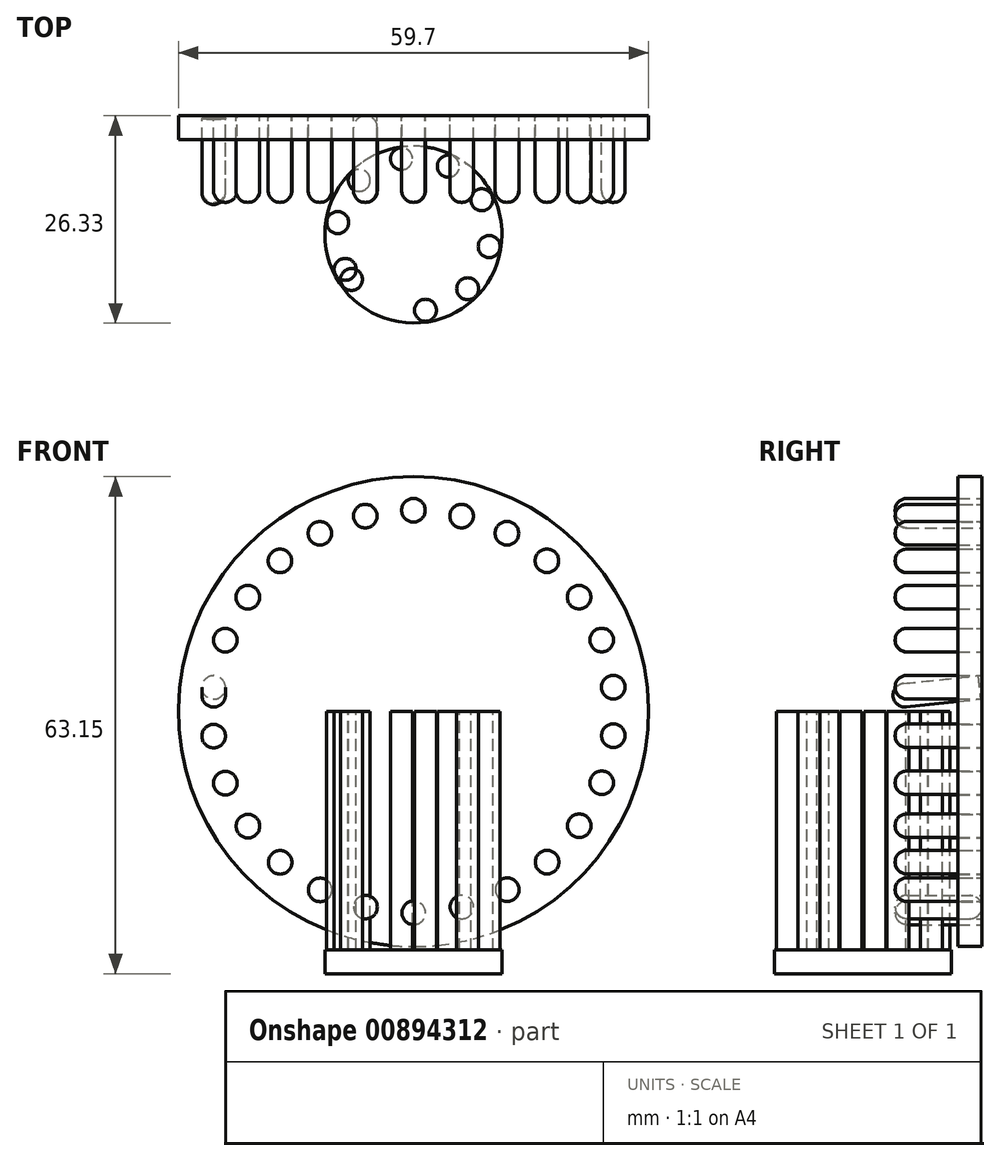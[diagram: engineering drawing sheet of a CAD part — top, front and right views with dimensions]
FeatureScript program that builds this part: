
annotation { "Feature Type Name" : "Feature", "Feature Type Description" : "" }
export const myFeature = defineFeature(function(context is Context, id is Id, definition is map)
    precondition{}
    {
        {
            var Q0;
            Q0=qCreatedBy(makeId("Front.planeOp"),FACE);
            var sketch = newSketch(context, id + "F0", { "sketchPlane" : qUnion([Q0])});
            skCircle(sketch, "E0", {"center": v(-25.57, 0) * mm, "radius": 1.5 * mm});
            skCircle(sketch, "E1.1.0", {"center": v(-25.38, 3.08) * mm, "radius": 1.5 * mm});
            skCircle(sketch, "E1.2.0", {"center": v(-24.83, 6.12) * mm, "radius": 1.5 * mm});
            skCircle(sketch, "E1.3.0", {"center": v(-23.91, 9.07) * mm, "radius": 1.5 * mm});
            skCircle(sketch, "E1.4.0", {"center": v(-22.64, 11.88) * mm, "radius": 1.5 * mm});
            skCircle(sketch, "E1.5.0", {"center": v(-21.05, 14.52) * mm, "radius": 1.5 * mm});
            skCircle(sketch, "E1.6.0", {"center": v(-19.14, 16.95) * mm, "radius": 1.5 * mm});
            skCircle(sketch, "E1.7.0", {"center": v(-16.96, 19.14) * mm, "radius": 1.5 * mm});
            skCircle(sketch, "E1.8.0", {"center": v(-14.53, 21.04) * mm, "radius": 1.5 * mm});
            skCircle(sketch, "E1.9.0", {"center": v(-11.89, 22.64) * mm, "radius": 1.5 * mm});
            skCircle(sketch, "E1.10.0", {"center": v(-9.07, 23.9) * mm, "radius": 1.5 * mm});
            skCircle(sketch, "E1.11.0", {"center": v(-6.13, 24.83) * mm, "radius": 1.5 * mm});
            skCircle(sketch, "E1.12.0", {"center": v(-3.1, 25.38) * mm, "radius": 1.5 * mm});
            skCircle(sketch, "E1.13.0", {"center": v(0, 25.57) * mm, "radius": 1.5 * mm});
            skCircle(sketch, "E1.14.0", {"center": v(3.07, 25.39) * mm, "radius": 1.5 * mm});
            skCircle(sketch, "E1.15.0", {"center": v(6.1, 24.83) * mm, "radius": 1.5 * mm});
            skCircle(sketch, "E1.16.0", {"center": v(9.06, 23.91) * mm, "radius": 1.5 * mm});
            skCircle(sketch, "E1.17.0", {"center": v(11.87, 22.65) * mm, "radius": 1.5 * mm});
            skCircle(sketch, "E1.18.0", {"center": v(14.52, 21.05) * mm, "radius": 1.5 * mm});
            skCircle(sketch, "E1.19.0", {"center": v(16.95, 19.15) * mm, "radius": 1.5 * mm});
            skCircle(sketch, "E1.20.0", {"center": v(19.13, 16.97) * mm, "radius": 1.5 * mm});
            skCircle(sketch, "E1.21.0", {"center": v(21.04, 14.54) * mm, "radius": 1.5 * mm});
            skCircle(sketch, "E1.22.0", {"center": v(22.64, 11.9) * mm, "radius": 1.5 * mm});
            skCircle(sketch, "E1.23.0", {"center": v(23.9, 9.08) * mm, "radius": 1.5 * mm});
            skCircle(sketch, "E1.24.0", {"center": v(24.82, 6.14) * mm, "radius": 1.5 * mm});
            skCircle(sketch, "E1.25.0", {"center": v(25.38, 3.1) * mm, "radius": 1.5 * mm});
            skCircle(sketch, "E1.26.0", {"center": v(25.57, 0.02) * mm, "radius": 1.5 * mm});
            skCircle(sketch, "E1.27.0", {"center": v(25.39, -3.06) * mm, "radius": 1.5 * mm});
            skCircle(sketch, "E1.28.0", {"center": v(24.83, -6.1) * mm, "radius": 1.5 * mm});
            skCircle(sketch, "E1.29.0", {"center": v(23.92, -9.05) * mm, "radius": 1.5 * mm});
            skCircle(sketch, "E1.30.0", {"center": v(22.65, -11.87) * mm, "radius": 1.5 * mm});
            skCircle(sketch, "E1.31.0", {"center": v(21.06, -14.5) * mm, "radius": 1.5 * mm});
            skCircle(sketch, "E1.32.0", {"center": v(19.15, -16.94) * mm, "radius": 1.5 * mm});
            skCircle(sketch, "E1.33.0", {"center": v(16.97, -19.13) * mm, "radius": 1.5 * mm});
            skCircle(sketch, "E1.34.0", {"center": v(14.54, -21.03) * mm, "radius": 1.5 * mm});
            skCircle(sketch, "E1.35.0", {"center": v(11.9, -22.63) * mm, "radius": 1.5 * mm});
            skCircle(sketch, "E1.36.0", {"center": v(9.1, -23.9) * mm, "radius": 1.5 * mm});
            skCircle(sketch, "E1.37.0", {"center": v(6.14, -24.82) * mm, "radius": 1.5 * mm});
            skCircle(sketch, "E1.38.0", {"center": v(3.1, -25.38) * mm, "radius": 1.5 * mm});
            skCircle(sketch, "E1.39.0", {"center": v(0.03, -25.57) * mm, "radius": 1.5 * mm});
            skCircle(sketch, "E1.40.0", {"center": v(-3.06, -25.39) * mm, "radius": 1.5 * mm});
            skCircle(sketch, "E1.41.0", {"center": v(-6.1, -24.83) * mm, "radius": 1.5 * mm});
            skCircle(sketch, "E1.42.0", {"center": v(-9.04, -23.92) * mm, "radius": 1.5 * mm});
            skCircle(sketch, "E1.43.0", {"center": v(-11.86, -22.66) * mm, "radius": 1.5 * mm});
            skCircle(sketch, "E1.44.0", {"center": v(-14.5, -21.06) * mm, "radius": 1.5 * mm});
            skCircle(sketch, "E1.45.0", {"center": v(-16.93, -19.16) * mm, "radius": 1.5 * mm});
            skCircle(sketch, "E1.46.0", {"center": v(-19.12, -16.98) * mm, "radius": 1.5 * mm});
            skCircle(sketch, "E1.47.0", {"center": v(-21.03, -14.55) * mm, "radius": 1.5 * mm});
            skCircle(sketch, "E1.48.0", {"center": v(-22.63, -11.91) * mm, "radius": 1.5 * mm});
            skCircle(sketch, "E1.49.0", {"center": v(-23.9, -9.1) * mm, "radius": 1.5 * mm});
            skCircle(sketch, "E1.50.0", {"center": v(-24.82, -6.15) * mm, "radius": 1.5 * mm});
            skLineSegment(sketch, "E1.anchor1", {"start": v(0, 0) * mm, "end": v(-25.57, 0) * mm, "construction": true});
            skLineSegment(sketch, "E1.anchor2", {"start": v(0, 0) * mm, "end": v(-25.38, -3.12) * mm, "construction": true});
            skCircle(sketch, "E2.1.51.0", {"center": v(-25.38, -3.12) * mm, "radius": 1.5 * mm});
            skCircle(sketch, "E3", {"center": v(0, 0) * mm, "radius": 29.85 * mm});
            skLineSegment(sketch, "E4", {"start": v(-29.85, 0) * mm, "end": v(29.85, 0.02) * mm});
            skSolve(sketch);
        }
        {
            var Q0;
            Q0=makeQuery(id+"F0.imprint","IMPRINT",FACE,{"disambiguationData":[TD([[makeQuery(id+"F0.imprint","IMPRINT",EDGE,{"derivedFrom":sQuery(id+"F0.wireOp",EDGE,"E1.1.0")}),1.0]])]});
            var Q1;
            Q1=makeQuery(id+"F0.imprint","IMPRINT",FACE,{"disambiguationData":[TD([[makeQuery(id+"F0.imprint","IMPRINT",EDGE,{"derivedFrom":sQuery(id+"F0.wireOp",EDGE,"E1.3.0")}),1.0]])]});
            var Q2;
            Q2=makeQuery(id+"F0.imprint","IMPRINT",FACE,{"disambiguationData":[TD([[makeQuery(id+"F0.imprint","IMPRINT",EDGE,{"derivedFrom":sQuery(id+"F0.wireOp",EDGE,"E1.5.0")}),1.0]])]});
            var Q3;
            Q3=makeQuery(id+"F0.imprint","IMPRINT",FACE,{"disambiguationData":[TD([[makeQuery(id+"F0.imprint","IMPRINT",EDGE,{"derivedFrom":sQuery(id+"F0.wireOp",EDGE,"E2.1.51.0")}),1.0]])]});
            var Q4;
            Q4=makeQuery(id+"F0.imprint","IMPRINT",FACE,{"disambiguationData":[TD([[makeQuery(id+"F0.imprint","IMPRINT",EDGE,{"derivedFrom":sQuery(id+"F0.wireOp",EDGE,"E1.49.0")}),1.0]])]});
            var Q5;
            Q5=makeQuery(id+"F0.imprint","IMPRINT",FACE,{"disambiguationData":[TD([[makeQuery(id+"F0.imprint","IMPRINT",EDGE,{"derivedFrom":sQuery(id+"F0.wireOp",EDGE,"E1.47.0")}),1.0]])]});
            var Q6;
            Q6=makeQuery(id+"F0.imprint","IMPRINT",FACE,{"disambiguationData":[TD([[makeQuery(id+"F0.imprint","IMPRINT",EDGE,{"derivedFrom":sQuery(id+"F0.wireOp",EDGE,"E1.45.0")}),1.0]])]});
            var Q7;
            Q7=makeQuery(id+"F0.imprint","IMPRINT",FACE,{"disambiguationData":[TD([[makeQuery(id+"F0.imprint","IMPRINT",EDGE,{"derivedFrom":sQuery(id+"F0.wireOp",EDGE,"E1.43.0")}),1.0]])]});
            var Q8;
            Q8=makeQuery(id+"F0.imprint","IMPRINT",FACE,{"disambiguationData":[TD([[makeQuery(id+"F0.imprint","IMPRINT",EDGE,{"derivedFrom":sQuery(id+"F0.wireOp",EDGE,"E1.41.0")}),1.0]])]});
            var Q9;
            Q9=makeQuery(id+"F0.imprint","IMPRINT",FACE,{"disambiguationData":[TD([[makeQuery(id+"F0.imprint","IMPRINT",EDGE,{"derivedFrom":sQuery(id+"F0.wireOp",EDGE,"E1.39.0")}),1.0]])]});
            var Q10;
            Q10=makeQuery(id+"F0.imprint","IMPRINT",FACE,{"disambiguationData":[TD([[makeQuery(id+"F0.imprint","IMPRINT",EDGE,{"derivedFrom":sQuery(id+"F0.wireOp",EDGE,"E1.37.0")}),1.0]])]});
            var Q11;
            Q11=makeQuery(id+"F0.imprint","IMPRINT",FACE,{"disambiguationData":[TD([[makeQuery(id+"F0.imprint","IMPRINT",EDGE,{"derivedFrom":sQuery(id+"F0.wireOp",EDGE,"E1.35.0")}),1.0]])]});
            var Q12;
            Q12=makeQuery(id+"F0.imprint","IMPRINT",FACE,{"disambiguationData":[TD([[makeQuery(id+"F0.imprint","IMPRINT",EDGE,{"derivedFrom":sQuery(id+"F0.wireOp",EDGE,"E1.33.0")}),1.0]])]});
            var Q13;
            Q13=makeQuery(id+"F0.imprint","IMPRINT",FACE,{"disambiguationData":[TD([[makeQuery(id+"F0.imprint","IMPRINT",EDGE,{"derivedFrom":sQuery(id+"F0.wireOp",EDGE,"E1.31.0")}),1.0]])]});
            var Q14;
            Q14=makeQuery(id+"F0.imprint","IMPRINT",FACE,{"disambiguationData":[TD([[makeQuery(id+"F0.imprint","IMPRINT",EDGE,{"derivedFrom":sQuery(id+"F0.wireOp",EDGE,"E1.29.0")}),1.0]])]});
            var Q15;
            Q15=makeQuery(id+"F0.imprint","IMPRINT",FACE,{"disambiguationData":[TD([[makeQuery(id+"F0.imprint","IMPRINT",EDGE,{"derivedFrom":sQuery(id+"F0.wireOp",EDGE,"E1.27.0")}),1.0]])]});
            var Q16;
            Q16=makeQuery(id+"F0.imprint","IMPRINT",FACE,{"disambiguationData":[TD([[makeQuery(id+"F0.imprint","IMPRINT",EDGE,{"derivedFrom":sQuery(id+"F0.wireOp",EDGE,"E1.25.0")}),1.0]])]});
            var Q17;
            Q17=makeQuery(id+"F0.imprint","IMPRINT",FACE,{"disambiguationData":[TD([[makeQuery(id+"F0.imprint","IMPRINT",EDGE,{"derivedFrom":sQuery(id+"F0.wireOp",EDGE,"E1.23.0")}),1.0]])]});
            var Q18;
            Q18=makeQuery(id+"F0.imprint","IMPRINT",FACE,{"disambiguationData":[TD([[makeQuery(id+"F0.imprint","IMPRINT",EDGE,{"derivedFrom":sQuery(id+"F0.wireOp",EDGE,"E1.21.0")}),1.0]])]});
            var Q19;
            Q19=makeQuery(id+"F0.imprint","IMPRINT",FACE,{"disambiguationData":[TD([[makeQuery(id+"F0.imprint","IMPRINT",EDGE,{"derivedFrom":sQuery(id+"F0.wireOp",EDGE,"E1.19.0")}),1.0]])]});
            var Q20;
            Q20=makeQuery(id+"F0.imprint","IMPRINT",FACE,{"disambiguationData":[TD([[makeQuery(id+"F0.imprint","IMPRINT",EDGE,{"derivedFrom":sQuery(id+"F0.wireOp",EDGE,"E1.17.0")}),1.0]])]});
            var Q21;
            Q21=makeQuery(id+"F0.imprint","IMPRINT",FACE,{"disambiguationData":[TD([[makeQuery(id+"F0.imprint","IMPRINT",EDGE,{"derivedFrom":sQuery(id+"F0.wireOp",EDGE,"E1.15.0")}),1.0]])]});
            var Q22;
            Q22=makeQuery(id+"F0.imprint","IMPRINT",FACE,{"disambiguationData":[TD([[makeQuery(id+"F0.imprint","IMPRINT",EDGE,{"derivedFrom":sQuery(id+"F0.wireOp",EDGE,"E1.13.0")}),1.0]])]});
            var Q23;
            Q23=makeQuery(id+"F0.imprint","IMPRINT",FACE,{"disambiguationData":[TD([[makeQuery(id+"F0.imprint","IMPRINT",EDGE,{"derivedFrom":sQuery(id+"F0.wireOp",EDGE,"E1.11.0")}),1.0]])]});
            var Q24;
            Q24=makeQuery(id+"F0.imprint","IMPRINT",FACE,{"disambiguationData":[TD([[makeQuery(id+"F0.imprint","IMPRINT",EDGE,{"derivedFrom":sQuery(id+"F0.wireOp",EDGE,"E1.9.0")}),1.0]])]});
            var Q25;
            Q25=makeQuery(id+"F0.imprint","IMPRINT",FACE,{"disambiguationData":[TD([[makeQuery(id+"F0.imprint","IMPRINT",EDGE,{"derivedFrom":sQuery(id+"F0.wireOp",EDGE,"E1.7.0")}),1.0]])]});
            extrude(context, id + "F1", {"entities" : qUnion([Q0, Q1, Q2, Q3, Q4, Q5, Q6, Q7, Q8, Q9, Q10, Q11, Q12, Q13, Q14, Q15, Q16, Q17, Q18, Q19, Q20, Q21, Q22, Q23, Q24, Q25]), "depth" : 11 * mm, "offsetDistance" : 25 * mm});
        }
        {
            var Q0;
            Q0=makeQuery(id+"F0.imprint","IMPRINT",FACE,{"disambiguationData":[TD([[makeQuery(id+"F0.imprint","IMPRINT",EDGE,{"derivedFrom":sQuery(id+"F0.wireOp",EDGE,"E0")}),-1.0]])]});
            var Q1;
            Q1=makeQuery(id+"F0.imprint","IMPRINT",FACE,{"disambiguationData":[TD([[makeQuery(id+"F0.imprint","IMPRINT",EDGE,{"derivedFrom":sQuery(id+"F0.wireOp",EDGE,"E1.50.0")}),1.0]])]});
            var Q2;
            Q2=makeQuery(id+"F0.imprint","IMPRINT",FACE,{"disambiguationData":[TD([[makeQuery(id+"F0.imprint","IMPRINT",EDGE,{"derivedFrom":sQuery(id+"F0.wireOp",EDGE,"E2.1.51.0")}),1.0]])]});
            var Q3;
            Q3=makeQuery(id+"F0.imprint","IMPRINT",FACE,{"disambiguationData":[TD([[makeQuery(id+"F0.imprint","IMPRINT",EDGE,{"derivedFrom":sQuery(id+"F0.wireOp",EDGE,"E0")}),1.0]])]});
            var Q4;
            Q4=makeQuery(id+"F0.imprint","IMPRINT",FACE,{"disambiguationData":[TD([[makeQuery(id+"F0.imprint","IMPRINT",EDGE,{"derivedFrom":sQuery(id+"F0.wireOp",EDGE,"E1.1.0")}),1.0]])]});
            var Q5;
            Q5=makeQuery(id+"F0.imprint","IMPRINT",FACE,{"disambiguationData":[TD([[makeQuery(id+"F0.imprint","IMPRINT",EDGE,{"derivedFrom":sQuery(id+"F0.wireOp",EDGE,"E1.2.0")}),1.0]])]});
            var Q6;
            Q6=makeQuery(id+"F0.imprint","IMPRINT",FACE,{"disambiguationData":[TD([[makeQuery(id+"F0.imprint","IMPRINT",EDGE,{"derivedFrom":sQuery(id+"F0.wireOp",EDGE,"E1.49.0")}),1.0]])]});
            var Q7;
            Q7=makeQuery(id+"F0.imprint","IMPRINT",FACE,{"disambiguationData":[TD([[makeQuery(id+"F0.imprint","IMPRINT",EDGE,{"derivedFrom":sQuery(id+"F0.wireOp",EDGE,"E1.48.0")}),1.0]])]});
            var Q8;
            Q8=makeQuery(id+"F0.imprint","IMPRINT",FACE,{"disambiguationData":[TD([[makeQuery(id+"F0.imprint","IMPRINT",EDGE,{"derivedFrom":sQuery(id+"F0.wireOp",EDGE,"E1.47.0")}),1.0]])]});
            var Q9;
            Q9=makeQuery(id+"F0.imprint","IMPRINT",FACE,{"disambiguationData":[TD([[makeQuery(id+"F0.imprint","IMPRINT",EDGE,{"derivedFrom":sQuery(id+"F0.wireOp",EDGE,"E1.46.0")}),1.0]])]});
            var Q10;
            Q10=makeQuery(id+"F0.imprint","IMPRINT",FACE,{"disambiguationData":[TD([[makeQuery(id+"F0.imprint","IMPRINT",EDGE,{"derivedFrom":sQuery(id+"F0.wireOp",EDGE,"E1.45.0")}),1.0]])]});
            var Q11;
            Q11=makeQuery(id+"F0.imprint","IMPRINT",FACE,{"disambiguationData":[TD([[makeQuery(id+"F0.imprint","IMPRINT",EDGE,{"derivedFrom":sQuery(id+"F0.wireOp",EDGE,"E1.44.0")}),1.0]])]});
            var Q12;
            Q12=makeQuery(id+"F0.imprint","IMPRINT",FACE,{"disambiguationData":[TD([[makeQuery(id+"F0.imprint","IMPRINT",EDGE,{"derivedFrom":sQuery(id+"F0.wireOp",EDGE,"E1.43.0")}),1.0]])]});
            var Q13;
            Q13=makeQuery(id+"F0.imprint","IMPRINT",FACE,{"disambiguationData":[TD([[makeQuery(id+"F0.imprint","IMPRINT",EDGE,{"derivedFrom":sQuery(id+"F0.wireOp",EDGE,"E1.42.0")}),1.0]])]});
            var Q14;
            Q14=makeQuery(id+"F0.imprint","IMPRINT",FACE,{"disambiguationData":[TD([[makeQuery(id+"F0.imprint","IMPRINT",EDGE,{"derivedFrom":sQuery(id+"F0.wireOp",EDGE,"E1.41.0")}),1.0]])]});
            var Q15;
            Q15=makeQuery(id+"F0.imprint","IMPRINT",FACE,{"disambiguationData":[TD([[makeQuery(id+"F0.imprint","IMPRINT",EDGE,{"derivedFrom":sQuery(id+"F0.wireOp",EDGE,"E1.40.0")}),1.0]])]});
            var Q16;
            Q16=makeQuery(id+"F0.imprint","IMPRINT",FACE,{"disambiguationData":[TD([[makeQuery(id+"F0.imprint","IMPRINT",EDGE,{"derivedFrom":sQuery(id+"F0.wireOp",EDGE,"E1.39.0")}),1.0]])]});
            var Q17;
            Q17=makeQuery(id+"F0.imprint","IMPRINT",FACE,{"disambiguationData":[TD([[makeQuery(id+"F0.imprint","IMPRINT",EDGE,{"derivedFrom":sQuery(id+"F0.wireOp",EDGE,"E1.38.0")}),1.0]])]});
            var Q18;
            Q18=makeQuery(id+"F0.imprint","IMPRINT",FACE,{"disambiguationData":[TD([[makeQuery(id+"F0.imprint","IMPRINT",EDGE,{"derivedFrom":sQuery(id+"F0.wireOp",EDGE,"E1.37.0")}),1.0]])]});
            var Q19;
            Q19=makeQuery(id+"F0.imprint","IMPRINT",FACE,{"disambiguationData":[TD([[makeQuery(id+"F0.imprint","IMPRINT",EDGE,{"derivedFrom":sQuery(id+"F0.wireOp",EDGE,"E1.36.0")}),1.0]])]});
            var Q20;
            Q20=makeQuery(id+"F0.imprint","IMPRINT",FACE,{"disambiguationData":[TD([[makeQuery(id+"F0.imprint","IMPRINT",EDGE,{"derivedFrom":sQuery(id+"F0.wireOp",EDGE,"E1.35.0")}),1.0]])]});
            var Q21;
            Q21=makeQuery(id+"F0.imprint","IMPRINT",FACE,{"disambiguationData":[TD([[makeQuery(id+"F0.imprint","IMPRINT",EDGE,{"derivedFrom":sQuery(id+"F0.wireOp",EDGE,"E1.34.0")}),1.0]])]});
            var Q22;
            Q22=makeQuery(id+"F0.imprint","IMPRINT",FACE,{"disambiguationData":[TD([[makeQuery(id+"F0.imprint","IMPRINT",EDGE,{"derivedFrom":sQuery(id+"F0.wireOp",EDGE,"E1.33.0")}),1.0]])]});
            var Q23;
            Q23=makeQuery(id+"F0.imprint","IMPRINT",FACE,{"disambiguationData":[TD([[makeQuery(id+"F0.imprint","IMPRINT",EDGE,{"derivedFrom":sQuery(id+"F0.wireOp",EDGE,"E1.32.0")}),1.0]])]});
            var Q24;
            Q24=makeQuery(id+"F0.imprint","IMPRINT",FACE,{"disambiguationData":[TD([[makeQuery(id+"F0.imprint","IMPRINT",EDGE,{"derivedFrom":sQuery(id+"F0.wireOp",EDGE,"E1.31.0")}),1.0]])]});
            var Q25;
            Q25=makeQuery(id+"F0.imprint","IMPRINT",FACE,{"disambiguationData":[TD([[makeQuery(id+"F0.imprint","IMPRINT",EDGE,{"derivedFrom":sQuery(id+"F0.wireOp",EDGE,"E1.30.0")}),1.0]])]});
            var Q26;
            Q26=makeQuery(id+"F0.imprint","IMPRINT",FACE,{"disambiguationData":[TD([[makeQuery(id+"F0.imprint","IMPRINT",EDGE,{"derivedFrom":sQuery(id+"F0.wireOp",EDGE,"E1.29.0")}),1.0]])]});
            var Q27;
            Q27=makeQuery(id+"F0.imprint","IMPRINT",FACE,{"disambiguationData":[TD([[makeQuery(id+"F0.imprint","IMPRINT",EDGE,{"derivedFrom":sQuery(id+"F0.wireOp",EDGE,"E1.28.0")}),1.0]])]});
            var Q28;
            Q28=makeQuery(id+"F0.imprint","IMPRINT",FACE,{"disambiguationData":[TD([[makeQuery(id+"F0.imprint","IMPRINT",EDGE,{"derivedFrom":sQuery(id+"F0.wireOp",EDGE,"E1.27.0")}),1.0]])]});
            var Q29;
            Q29=makeQuery(id+"F0.imprint","IMPRINT",FACE,{"disambiguationData":[TD([[makeQuery(id+"F0.imprint","IMPRINT",EDGE,{"derivedFrom":sQuery(id+"F0.wireOp",EDGE,"E1.26.0")}),1.0]])]});
            var Q30;
            Q30=makeQuery(id+"F0.imprint","IMPRINT",FACE,{"disambiguationData":[TD([[makeQuery(id+"F0.imprint","IMPRINT",EDGE,{"derivedFrom":sQuery(id+"F0.wireOp",EDGE,"E1.25.0")}),1.0]])]});
            var Q31;
            Q31=makeQuery(id+"F0.imprint","IMPRINT",FACE,{"disambiguationData":[TD([[makeQuery(id+"F0.imprint","IMPRINT",EDGE,{"derivedFrom":sQuery(id+"F0.wireOp",EDGE,"E1.24.0")}),1.0]])]});
            var Q32;
            Q32=makeQuery(id+"F0.imprint","IMPRINT",FACE,{"disambiguationData":[TD([[makeQuery(id+"F0.imprint","IMPRINT",EDGE,{"derivedFrom":sQuery(id+"F0.wireOp",EDGE,"E1.23.0")}),1.0]])]});
            var Q33;
            Q33=makeQuery(id+"F0.imprint","IMPRINT",FACE,{"disambiguationData":[TD([[makeQuery(id+"F0.imprint","IMPRINT",EDGE,{"derivedFrom":sQuery(id+"F0.wireOp",EDGE,"E1.22.0")}),1.0]])]});
            var Q34;
            Q34=makeQuery(id+"F0.imprint","IMPRINT",FACE,{"disambiguationData":[TD([[makeQuery(id+"F0.imprint","IMPRINT",EDGE,{"derivedFrom":sQuery(id+"F0.wireOp",EDGE,"E1.21.0")}),1.0]])]});
            var Q35;
            Q35=makeQuery(id+"F0.imprint","IMPRINT",FACE,{"disambiguationData":[TD([[makeQuery(id+"F0.imprint","IMPRINT",EDGE,{"derivedFrom":sQuery(id+"F0.wireOp",EDGE,"E1.20.0")}),1.0]])]});
            var Q36;
            Q36=makeQuery(id+"F0.imprint","IMPRINT",FACE,{"disambiguationData":[TD([[makeQuery(id+"F0.imprint","IMPRINT",EDGE,{"derivedFrom":sQuery(id+"F0.wireOp",EDGE,"E1.19.0")}),1.0]])]});
            var Q37;
            Q37=makeQuery(id+"F0.imprint","IMPRINT",FACE,{"disambiguationData":[TD([[makeQuery(id+"F0.imprint","IMPRINT",EDGE,{"derivedFrom":sQuery(id+"F0.wireOp",EDGE,"E1.18.0")}),1.0]])]});
            var Q38;
            Q38=makeQuery(id+"F0.imprint","IMPRINT",FACE,{"disambiguationData":[TD([[makeQuery(id+"F0.imprint","IMPRINT",EDGE,{"derivedFrom":sQuery(id+"F0.wireOp",EDGE,"E1.17.0")}),1.0]])]});
            var Q39;
            Q39=makeQuery(id+"F0.imprint","IMPRINT",FACE,{"disambiguationData":[TD([[makeQuery(id+"F0.imprint","IMPRINT",EDGE,{"derivedFrom":sQuery(id+"F0.wireOp",EDGE,"E1.16.0")}),1.0]])]});
            var Q40;
            Q40=makeQuery(id+"F0.imprint","IMPRINT",FACE,{"disambiguationData":[TD([[makeQuery(id+"F0.imprint","IMPRINT",EDGE,{"derivedFrom":sQuery(id+"F0.wireOp",EDGE,"E1.15.0")}),1.0]])]});
            var Q41;
            Q41=makeQuery(id+"F0.imprint","IMPRINT",FACE,{"disambiguationData":[TD([[makeQuery(id+"F0.imprint","IMPRINT",EDGE,{"derivedFrom":sQuery(id+"F0.wireOp",EDGE,"E1.14.0")}),1.0]])]});
            var Q42;
            Q42=makeQuery(id+"F0.imprint","IMPRINT",FACE,{"disambiguationData":[TD([[makeQuery(id+"F0.imprint","IMPRINT",EDGE,{"derivedFrom":sQuery(id+"F0.wireOp",EDGE,"E1.13.0")}),1.0]])]});
            var Q43;
            Q43=makeQuery(id+"F0.imprint","IMPRINT",FACE,{"disambiguationData":[TD([[makeQuery(id+"F0.imprint","IMPRINT",EDGE,{"derivedFrom":sQuery(id+"F0.wireOp",EDGE,"E1.12.0")}),1.0]])]});
            var Q44;
            Q44=makeQuery(id+"F0.imprint","IMPRINT",FACE,{"disambiguationData":[TD([[makeQuery(id+"F0.imprint","IMPRINT",EDGE,{"derivedFrom":sQuery(id+"F0.wireOp",EDGE,"E1.11.0")}),1.0]])]});
            var Q45;
            Q45=makeQuery(id+"F0.imprint","IMPRINT",FACE,{"disambiguationData":[TD([[makeQuery(id+"F0.imprint","IMPRINT",EDGE,{"derivedFrom":sQuery(id+"F0.wireOp",EDGE,"E1.10.0")}),1.0]])]});
            var Q46;
            Q46=makeQuery(id+"F0.imprint","IMPRINT",FACE,{"disambiguationData":[TD([[makeQuery(id+"F0.imprint","IMPRINT",EDGE,{"derivedFrom":sQuery(id+"F0.wireOp",EDGE,"E1.9.0")}),1.0]])]});
            var Q47;
            Q47=makeQuery(id+"F0.imprint","IMPRINT",FACE,{"disambiguationData":[TD([[makeQuery(id+"F0.imprint","IMPRINT",EDGE,{"derivedFrom":sQuery(id+"F0.wireOp",EDGE,"E1.8.0")}),1.0]])]});
            var Q48;
            Q48=makeQuery(id+"F0.imprint","IMPRINT",FACE,{"disambiguationData":[TD([[makeQuery(id+"F0.imprint","IMPRINT",EDGE,{"derivedFrom":sQuery(id+"F0.wireOp",EDGE,"E1.7.0")}),1.0]])]});
            var Q49;
            Q49=makeQuery(id+"F0.imprint","IMPRINT",FACE,{"disambiguationData":[TD([[makeQuery(id+"F0.imprint","IMPRINT",EDGE,{"derivedFrom":sQuery(id+"F0.wireOp",EDGE,"E1.6.0")}),1.0]])]});
            var Q50;
            Q50=makeQuery(id+"F0.imprint","IMPRINT",FACE,{"disambiguationData":[TD([[makeQuery(id+"F0.imprint","IMPRINT",EDGE,{"derivedFrom":sQuery(id+"F0.wireOp",EDGE,"E1.5.0")}),1.0]])]});
            var Q51;
            Q51=makeQuery(id+"F0.imprint","IMPRINT",FACE,{"disambiguationData":[TD([[makeQuery(id+"F0.imprint","IMPRINT",EDGE,{"derivedFrom":sQuery(id+"F0.wireOp",EDGE,"E1.4.0")}),1.0]])]});
            var Q52;
            Q52=makeQuery(id+"F0.imprint","IMPRINT",FACE,{"disambiguationData":[TD([[makeQuery(id+"F0.imprint","IMPRINT",EDGE,{"derivedFrom":sQuery(id+"F0.wireOp",EDGE,"E1.3.0")}),1.0]])]});
            extrude(context, id + "F2", {"entities" : qUnion([Q0, Q1, Q2, Q3, Q4, Q5, Q6, Q7, Q8, Q9, Q10, Q11, Q12, Q13, Q14, Q15, Q16, Q17, Q18, Q19, Q20, Q21, Q22, Q23, Q24, Q25, Q26, Q27, Q28, Q29, Q30, Q31, Q32, Q33, Q34, Q35, Q36, Q37, Q38, Q39, Q40, Q41, Q42, Q43, Q44, Q45, Q46, Q47, Q48, Q49, Q50, Q51, Q52]), "depth" : 3 * mm, "offsetDistance" : 25 * mm});
        }
        {
            var Q0;
            Q0=makeQuery(id+"F1.opExtrude","CAP_EDGE",EDGE,{"disambiguationData":[OSD([sQuery(id+"F0.wireOp",EDGE,"E1.25.0")])],"isStart":false});
            var Q1;
            Q1=makeQuery(id+"F1.opExtrude","CAP_EDGE",EDGE,{"disambiguationData":[OSD([sQuery(id+"F0.wireOp",EDGE,"E1.23.0")])],"isStart":false});
            var Q2;
            Q2=makeQuery(id+"F1.opExtrude","CAP_EDGE",EDGE,{"disambiguationData":[OSD([sQuery(id+"F0.wireOp",EDGE,"E1.21.0")])],"isStart":false});
            var Q3;
            Q3=makeQuery(id+"F1.opExtrude","CAP_EDGE",EDGE,{"disambiguationData":[OSD([sQuery(id+"F0.wireOp",EDGE,"E1.27.0")])],"isStart":false});
            var Q4;
            Q4=makeQuery(id+"F1.opExtrude","CAP_EDGE",EDGE,{"disambiguationData":[OSD([sQuery(id+"F0.wireOp",EDGE,"E1.29.0")])],"isStart":false});
            var Q5;
            Q5=makeQuery(id+"F1.opExtrude","CAP_EDGE",EDGE,{"disambiguationData":[OSD([sQuery(id+"F0.wireOp",EDGE,"E1.31.0")])],"isStart":false});
            var Q6;
            Q6=makeQuery(id+"F1.opExtrude","CAP_EDGE",EDGE,{"disambiguationData":[OSD([sQuery(id+"F0.wireOp",EDGE,"E1.33.0")])],"isStart":false});
            var Q7;
            Q7=makeQuery(id+"F1.opExtrude","CAP_EDGE",EDGE,{"disambiguationData":[OSD([sQuery(id+"F0.wireOp",EDGE,"E1.35.0")])],"isStart":false});
            var Q8;
            Q8=makeQuery(id+"F1.opExtrude","CAP_EDGE",EDGE,{"disambiguationData":[OSD([sQuery(id+"F0.wireOp",EDGE,"E1.37.0")])],"isStart":false});
            var Q9;
            Q9=makeQuery(id+"F1.opExtrude","CAP_EDGE",EDGE,{"disambiguationData":[OSD([sQuery(id+"F0.wireOp",EDGE,"E1.39.0")])],"isStart":false});
            var Q10;
            Q10=makeQuery(id+"F1.opExtrude","SWEPT_FACE",FACE,{"disambiguationData":[OSD([sQuery(id+"F0.wireOp",EDGE,"E1.41.0")])]});
            var Q11;
            Q11=makeQuery(id+"F1.opExtrude","CAP_EDGE",EDGE,{"disambiguationData":[OSD([sQuery(id+"F0.wireOp",EDGE,"E1.43.0")])],"isStart":false});
            var Q12;
            Q12=makeQuery(id+"F1.opExtrude","CAP_EDGE",EDGE,{"disambiguationData":[OSD([sQuery(id+"F0.wireOp",EDGE,"E1.45.0")])],"isStart":false});
            var Q13;
            Q13=makeQuery(id+"F1.opExtrude","CAP_EDGE",EDGE,{"disambiguationData":[OSD([sQuery(id+"F0.wireOp",EDGE,"E1.47.0")])],"isStart":false});
            var Q14;
            Q14=makeQuery(id+"F1.opExtrude","CAP_EDGE",EDGE,{"disambiguationData":[OSD([sQuery(id+"F0.wireOp",EDGE,"E1.49.0")])],"isStart":false});
            var Q15;
            Q15=makeQuery(id+"F1.opExtrude","CAP_EDGE",EDGE,{"disambiguationData":[OSD([sQuery(id+"F0.wireOp",EDGE,"E2.1.51.0")])],"isStart":false});
            var Q16;
            Q16=makeQuery(id+"F1.opExtrude","CAP_EDGE",EDGE,{"disambiguationData":[OSD([sQuery(id+"F0.wireOp",EDGE,"E1.1.0")])],"isStart":false});
            var Q17;
            Q17=makeQuery(id+"F1.opExtrude","CAP_EDGE",EDGE,{"disambiguationData":[OSD([sQuery(id+"F0.wireOp",EDGE,"E1.3.0")])],"isStart":false});
            var Q18;
            Q18=makeQuery(id+"F1.opExtrude","CAP_EDGE",EDGE,{"disambiguationData":[OSD([sQuery(id+"F0.wireOp",EDGE,"E1.5.0")])],"isStart":false});
            var Q19;
            Q19=makeQuery(id+"F1.opExtrude","CAP_EDGE",EDGE,{"disambiguationData":[OSD([sQuery(id+"F0.wireOp",EDGE,"E1.7.0")])],"isStart":false});
            var Q20;
            Q20=makeQuery(id+"F1.opExtrude","CAP_EDGE",EDGE,{"disambiguationData":[OSD([sQuery(id+"F0.wireOp",EDGE,"E1.9.0")])],"isStart":false});
            var Q21;
            Q21=makeQuery(id+"F1.opExtrude","CAP_EDGE",EDGE,{"disambiguationData":[OSD([sQuery(id+"F0.wireOp",EDGE,"E1.11.0")])],"isStart":false});
            var Q22;
            Q22=makeQuery(id+"F1.opExtrude","CAP_EDGE",EDGE,{"disambiguationData":[OSD([sQuery(id+"F0.wireOp",EDGE,"E1.13.0")])],"isStart":false});
            var Q23;
            Q23=makeQuery(id+"F1.opExtrude","CAP_EDGE",EDGE,{"disambiguationData":[OSD([sQuery(id+"F0.wireOp",EDGE,"E1.15.0")])],"isStart":false});
            var Q24;
            Q24=makeQuery(id+"F1.opExtrude","CAP_EDGE",EDGE,{"disambiguationData":[OSD([sQuery(id+"F0.wireOp",EDGE,"E1.17.0")])],"isStart":false});
            var Q25;
            Q25=makeQuery(id+"F1.opExtrude","CAP_EDGE",EDGE,{"disambiguationData":[OSD([sQuery(id+"F0.wireOp",EDGE,"E1.19.0")])],"isStart":false});
            fillet(context, id + "F3", {"entities" : qUnion([Q0, Q1, Q2, Q3, Q4, Q5, Q6, Q7, Q8, Q9, Q10, Q11, Q12, Q13, Q14, Q15, Q16, Q17, Q18, Q19, Q20, Q21, Q22, Q23, Q24, Q25]), "radius" : 1.5 * mm, "tangentPropagation" : true, "allowEdgeOverflow" : false});
        }
        {
            var Q0;
            Q0=makeQuery(id+"F1.opExtrude","SWEPT_BODY",BODY,{"disambiguationData":[OSD([sQuery(id+"F0.wireOp",EDGE,"E1.1.0")])]});
            var Q1;
            Q1=sQuery(id+"F0.wireOp",EDGE,"E4");
            transform(context, id + "F4", {"entities" : qUnion([Q0]), "transformType" : TransformType.ROTATION, "transformAxis" : qUnion([Q1]), "angle" : 6 * degree, "makeCopy" : false});
        }
        {
            var Q0;
            Q0=qCreatedBy(makeId("Top.planeOp"),FACE);
            var sketch = newSketch(context, id + "F5", { "sketchPlane" : qUnion([Q0])});
            skCircle(sketch, "E5", {"center": v(0, -17.79) * mm, "radius": 11.24 * mm});
            skSolve(sketch);
        }
        {
            var Q0;
            Q0=makeQuery(id+"F5.imprint","IMPRINT",FACE,{"disambiguationData":[TD([[makeQuery(id+"F5.imprint","IMPRINT",EDGE,{"derivedFrom":sQuery(id+"F5.wireOp",EDGE,"E5")}),1.0]])]});
            extrude(context, id + "F6", {"entities" : qUnion([Q0]), "depth" : 3 * mm, "offsetDistance" : 25 * mm});
        }
        {
            var Q0;
            Q0=makeQuery(id+"F6.opExtrude","SWEPT_BODY",BODY,{"disambiguationData":[OSD([sQuery(id+"F5.wireOp",EDGE,"E5")])]});
            transform(context, id + "F7", {"entities" : qUnion([Q0]), "transformType" : TransformType.TRANSLATION_3D, "dx" : 0 * mm, "dy" : 2.7 * mm, "dz" : -33.3 * mm, "makeCopy" : false});
        }
        {
            var Q0;
            Q0=qCreatedBy(makeId("Top.planeOp"),FACE);
            var sketch = newSketch(context, id + "F8", { "sketchPlane" : qUnion([Q0])});
            skPoint(sketch, "E6.center", {"position": v(0, -15.09) * mm});
            skCircle(sketch, "E7.0", {"center": v(0, -15.09) * mm, "radius": 9.74 * mm, "construction": true});
            skCircle(sketch, "E8", {"center": v(-4.42, -23.76) * mm, "radius": 1.4 * mm});
            skCircle(sketch, "E9.1.0", {"center": v(-8.68, -19.5) * mm, "radius": 1.4 * mm});
            skCircle(sketch, "E9.2.0", {"center": v(-9.62, -13.56) * mm, "radius": 1.4 * mm});
            skCircle(sketch, "E9.3.0", {"center": v(-6.89, -8.2) * mm, "radius": 1.4 * mm});
            skCircle(sketch, "E9.4.0", {"center": v(-1.52, -5.46) * mm, "radius": 1.4 * mm});
            skLineSegment(sketch, "E9.anchor1", {"start": v(0, -15.09) * mm, "end": v(-4.42, -23.76) * mm, "construction": true});
            skLineSegment(sketch, "E9.anchor2", {"start": v(0, -15.09) * mm, "end": v(1.52, -24.7) * mm, "construction": true});
            skCircle(sketch, "E10.1.5.0", {"center": v(4.42, -6.4) * mm, "radius": 1.4 * mm});
            skCircle(sketch, "E10.1.6.0", {"center": v(8.68, -10.66) * mm, "radius": 1.4 * mm});
            skCircle(sketch, "E10.1.7.0", {"center": v(9.62, -16.6) * mm, "radius": 1.4 * mm});
            skCircle(sketch, "E10.1.8.0", {"center": v(6.89, -21.97) * mm, "radius": 1.4 * mm});
            skCircle(sketch, "E10.1.9.0", {"center": v(1.52, -24.7) * mm, "radius": 1.4 * mm});
            skSolve(sketch);
        }
        {
            var Q0;
            Q0=makeQuery(id+"F8.imprint","IMPRINT",FACE,{"disambiguationData":[TD([[makeQuery(id+"F8.imprint","IMPRINT",EDGE,{"derivedFrom":sQuery(id+"F8.wireOp",EDGE,"E9.3.0")}),1.0]])]});
            var Q1;
            Q1=makeQuery(id+"F8.imprint","IMPRINT",FACE,{"disambiguationData":[TD([[makeQuery(id+"F8.imprint","IMPRINT",EDGE,{"derivedFrom":sQuery(id+"F8.wireOp",EDGE,"E9.4.0")}),1.0]])]});
            var Q2;
            Q2=makeQuery(id+"F8.imprint","IMPRINT",FACE,{"disambiguationData":[TD([[makeQuery(id+"F8.imprint","IMPRINT",EDGE,{"derivedFrom":sQuery(id+"F8.wireOp",EDGE,"E10.1.5.0")}),1.0]])]});
            var Q3;
            Q3=makeQuery(id+"F8.imprint","IMPRINT",FACE,{"disambiguationData":[TD([[makeQuery(id+"F8.imprint","IMPRINT",EDGE,{"derivedFrom":sQuery(id+"F8.wireOp",EDGE,"E10.1.6.0")}),1.0]])]});
            var Q4;
            Q4=makeQuery(id+"F8.imprint","IMPRINT",FACE,{"disambiguationData":[TD([[makeQuery(id+"F8.imprint","IMPRINT",EDGE,{"derivedFrom":sQuery(id+"F8.wireOp",EDGE,"E10.1.7.0")}),1.0]])]});
            var Q5;
            Q5=makeQuery(id+"F8.imprint","IMPRINT",FACE,{"disambiguationData":[TD([[makeQuery(id+"F8.imprint","IMPRINT",EDGE,{"derivedFrom":sQuery(id+"F8.wireOp",EDGE,"E10.1.8.0")}),1.0]])]});
            var Q6;
            Q6=makeQuery(id+"F8.imprint","IMPRINT",FACE,{"disambiguationData":[TD([[makeQuery(id+"F8.imprint","IMPRINT",EDGE,{"derivedFrom":sQuery(id+"F8.wireOp",EDGE,"E10.1.9.0")}),1.0]])]});
            var Q7;
            Q7=makeQuery(id+"F8.imprint","IMPRINT",FACE,{"disambiguationData":[TD([[makeQuery(id+"F8.imprint","IMPRINT",EDGE,{"derivedFrom":sQuery(id+"F8.wireOp",EDGE,"E8")}),1.0]])]});
            var Q8;
            Q8=makeQuery(id+"F8.imprint","IMPRINT",FACE,{"disambiguationData":[TD([[makeQuery(id+"F8.imprint","IMPRINT",EDGE,{"derivedFrom":sQuery(id+"F8.wireOp",EDGE,"E9.1.0")}),1.0]])]});
            var Q9;
            Q9=makeQuery(id+"F8.imprint","IMPRINT",FACE,{"disambiguationData":[TD([[makeQuery(id+"F8.imprint","IMPRINT",EDGE,{"derivedFrom":sQuery(id+"F8.wireOp",EDGE,"E9.2.0")}),1.0]])]});
            extrude(context, id + "F9", {"entities" : qUnion([Q0, Q1, Q2, Q3, Q4, Q5, Q6, Q7, Q8, Q9]), "oppositeDirection" : true, "depth" : (25 + 5.3) * mm, "offsetDistance" : 25 * mm});
        }
        {
            var Q0;
            Q0=makeQuery(id+"F6.opExtrude","CAP_FACE",FACE,{"disambiguationData":[OSD([sQuery(id+"F5.wireOp",EDGE,"E5")])],"isStart":false});
            var sketch = newSketch(context, id + "F10", { "sketchPlane" : qUnion([Q0])});
            skPoint(sketch, "E11", {"position": v(0, -15.09) * mm});
            skSolve(sketch);
        }
        {
            var Q0;
            Q0=sQuery(id+"F8.wireOp",VERTEX,"E6.center");
            var Q1;
            Q1=sQuery(id+"F10.wireOp",VERTEX,"E11");
            var Q2;
            Q2=sQuery(id+"F8.wireOp",VERTEX,"E10.1.7.0.center");
            cPlane(context, id + "F11", {"entities" : qUnion([Q0, Q1, Q2]), "cplaneType" : CPlaneType.THREE_POINT, "offset" : 25 * mm, "width" : 150 * mm, "height" : 150 * mm});
        }
        {
            var Q0;
            Q0=qCreatedBy(id+"F11.planeOp",FACE);
            var sketch = newSketch(context, id + "F12", { "sketchPlane" : qUnion([Q0])});
            skLineSegment(sketch, "E12", {"start": v(-2.4, 0) * mm, "end": v(-2.4, -30.28) * mm, "construction": true});
            skSolve(sketch);
        }
        {
            var Q0;
            Q0=makeQuery(id+"F9.opExtrude","SWEPT_BODY",BODY,{"disambiguationData":[OSD([sQuery(id+"F8.wireOp",EDGE,"E8")])]});
            var Q1;
            Q1=sQuery(id+"F12.wireOp",EDGE,"E12");
            transform(context, id + "F13", {"entities" : qUnion([Q0]), "transformType" : TransformType.ROTATION, "transformAxis" : qUnion([Q1]), "angle" : 27 * degree, "makeCopy" : false});
        }
    });
